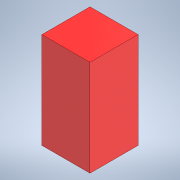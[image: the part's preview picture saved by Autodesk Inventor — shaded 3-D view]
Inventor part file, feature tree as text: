
AUTODESK INVENTOR PART (.ipt)
format: ipt  version: 2022.6 (Build 266554000, 554)  size: 90,112 bytes
history: native  units: mm
features: extrude x1, sketch x1
ambient origin geometry x8: Origin, YZ Plane, XZ Plane, XY Plane, X Axis, Y Axis, Z Axis, Center Point
bodies: Solid1 (feature_tree)
feature tree (2):
  extrude  "Extrusion1"  Depth=50.0mm
  sketch  "Sketch1"  dims[d0=100.0mm d1=50.0mm d2=50.0mm d3=0.0mm]
